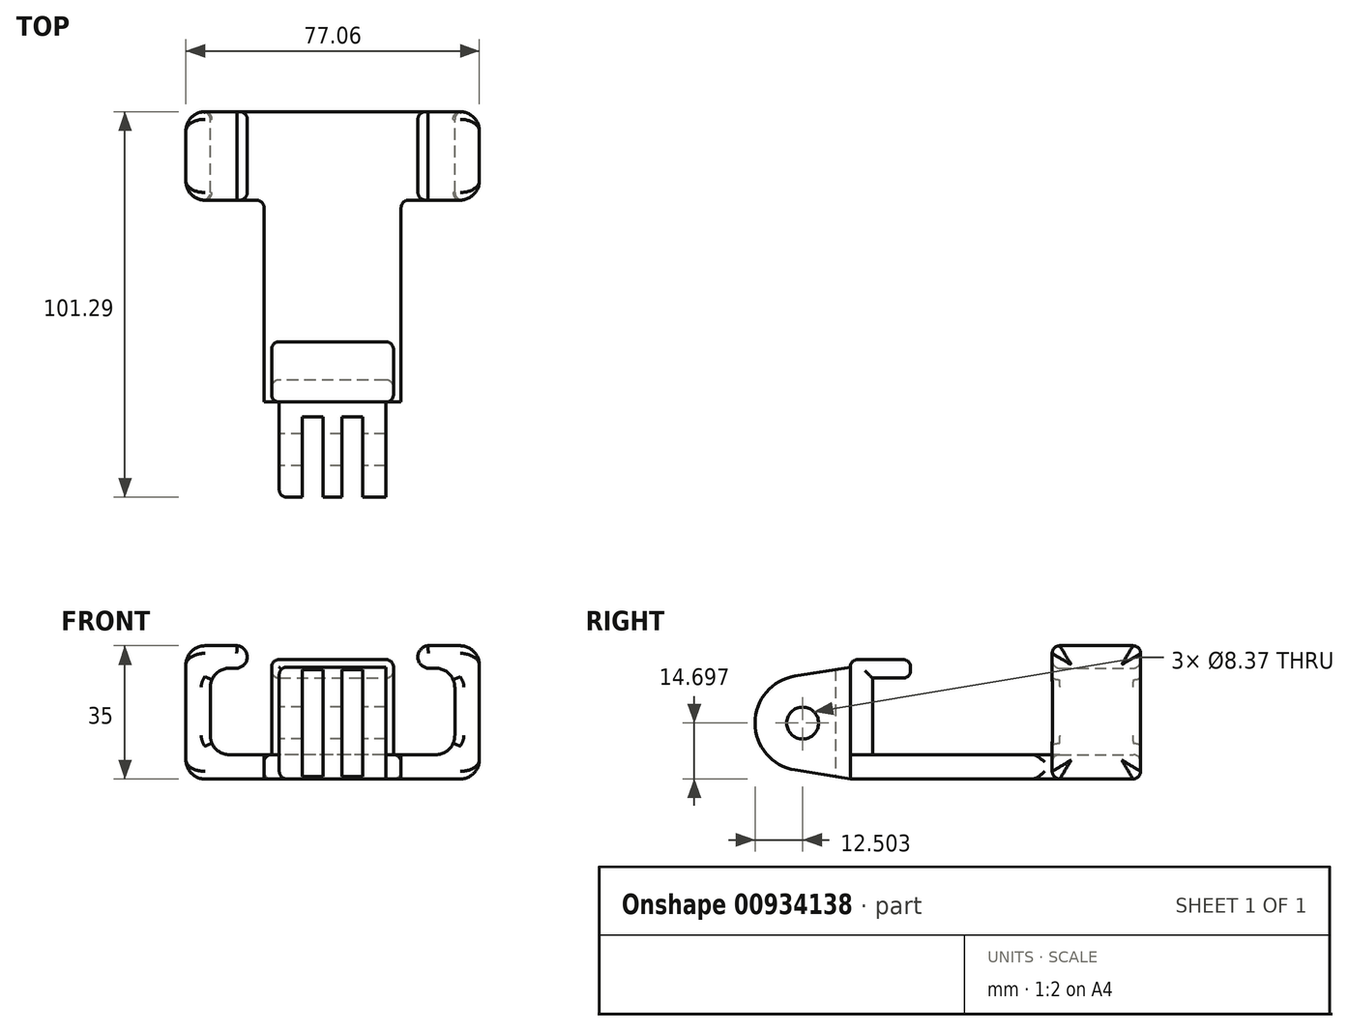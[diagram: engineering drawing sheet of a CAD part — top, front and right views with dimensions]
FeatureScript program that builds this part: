
annotation { "Feature Type Name" : "Feature", "Feature Type Description" : "" }
export const myFeature = defineFeature(function(context is Context, id is Id, definition is map)
    precondition{}
    {
        {
            var Q0;
            Q0=qCreatedBy(makeId("Top.planeOp"),FACE);
            var sketch = newSketch(context, id + "F0", { "sketchPlane" : qUnion([Q0])});
            skLineSegment(sketch, "E0", {"start": v(0, -65.26) * mm, "end": v(18, -65.26) * mm});
            skLineSegment(sketch, "E1", {"start": v(18, -65.26) * mm, "end": v(18, -12.2) * mm});
            skLineSegment(sketch, "E2", {"start": v(18, -12.2) * mm, "end": v(38.53, -12.2) * mm});
            skLineSegment(sketch, "E3", {"start": v(38.53, -12.2) * mm, "end": v(38.53, 11.03) * mm});
            skLineSegment(sketch, "E4", {"start": v(38.53, 11.03) * mm, "end": v(0, 11.03) * mm});
            skLineSegment(sketch, "E5.MirrorCS", {"start": v(-38.53, 11.03) * mm, "end": v(0, 11.03) * mm});
            skLineSegment(sketch, "E6.MirrorCS", {"start": v(-38.53, -12.2) * mm, "end": v(-38.53, 11.03) * mm});
            skLineSegment(sketch, "E7.MirrorCS", {"start": v(-18, -12.2) * mm, "end": v(-38.53, -12.2) * mm});
            skLineSegment(sketch, "E8.MirrorCS", {"start": v(-18, -65.26) * mm, "end": v(-18, -12.2) * mm});
            skLineSegment(sketch, "E9.MirrorCS", {"start": v(0, -65.26) * mm, "end": v(-18, -65.26) * mm});
            skSolve(sketch);
        }
        {
            var Q0;
            Q0=makeQuery(id+"F0.imprint","IMPRINT",FACE,{"disambiguationData":[TD([[makeQuery(id+"F0.imprint","IMPRINT",EDGE,{"derivedFrom":sQuery(id+"F0.wireOp",EDGE,"E0")}),1.0]])]});
            extrude(context, id + "F1", {"entities" : qUnion([Q0]), "depth" : 35 * mm, "offsetDistance" : 25 * mm});
        }
        {
            var Q0;
            Q0=makeQuery(id+"F1.opExtrude","SWEPT_FACE",FACE,{"disambiguationData":[OSD([sQuery(id+"F0.wireOp",EDGE,"E4"),sQuery(id+"F0.wireOp",EDGE,"E5.MirrorCS")])]});
            var sketch = newSketch(context, id + "F2", { "sketchPlane" : qUnion([Q0])});
            skLineSegment(sketch, "E10", {"start": v(-25.39, 29.08) * mm, "end": v(-27.11, 29.08) * mm});
            skLineSegment(sketch, "E11", {"start": v(-32.11, 24.08) * mm, "end": v(-32.11, 11.4) * mm});
            skLineSegment(sketch, "E12", {"start": v(-27.11, 6.4) * mm, "end": v(0, 6.4) * mm});
            skLineSegment(sketch, "E13.MirrorCS", {"start": v(32.11, 24.08) * mm, "end": v(32.11, 11.4) * mm});
            skLineSegment(sketch, "E14.MirrorCS", {"start": v(25.39, 29.08) * mm, "end": v(27.11, 29.08) * mm});
            skLineSegment(sketch, "E15.MirrorCS", {"start": v(27.11, 6.4) * mm, "end": v(0, 6.4) * mm});
            skArc(sketch, "E16", {"start": v(-25.39, 29.08) * mm, "mid": v(-22.43, 31.88) * mm, "end": v(-25.05, 35) * mm});
            skLineSegment(sketch, "E17", {"start": v(0, 0) * mm, "end": v(0, 33.52) * mm, "construction": true});
            skArc(sketch, "E18.MirrorCS", {"start": v(25.39, 29.08) * mm, "mid": v(22.43, 31.88) * mm, "end": v(25.05, 35) * mm});
            skPoint(sketch, "E19.visualSharp", {"position": v(-32.11, 29.08) * mm});
            skArc(sketch, "E19.filletArc", {"start": v(-27.11, 29.08) * mm, "mid": v(-30.65, 27.62) * mm, "end": v(-32.11, 24.08) * mm});
            skPoint(sketch, "E20.visualSharp", {"position": v(32.11, 29.08) * mm});
            skArc(sketch, "E20.filletArc", {"start": v(32.11, 24.08) * mm, "mid": v(30.65, 27.62) * mm, "end": v(27.11, 29.08) * mm});
            skPoint(sketch, "E21.visualSharp", {"position": v(32.11, 6.4) * mm});
            skArc(sketch, "E21.filletArc", {"start": v(27.11, 6.4) * mm, "mid": v(30.65, 7.86) * mm, "end": v(32.11, 11.4) * mm});
            skPoint(sketch, "E22.visualSharp", {"position": v(-32.11, 6.4) * mm});
            skArc(sketch, "E22.filletArc", {"start": v(-32.11, 11.4) * mm, "mid": v(-30.65, 7.86) * mm, "end": v(-27.11, 6.4) * mm});
            skLineSegment(sketch, "E23", {"start": v(25.05, 35) * mm, "end": v(30.53, 35) * mm});
            skLineSegment(sketch, "E24", {"start": v(38.53, 27) * mm, "end": v(38.53, 8) * mm});
            skLineSegment(sketch, "E25", {"start": v(30.53, 0) * mm, "end": v(0, 0) * mm});
            skLineSegment(sketch, "E26", {"start": v(0, 0) * mm, "end": v(-30.53, 0) * mm});
            skLineSegment(sketch, "E27", {"start": v(-38.53, 8) * mm, "end": v(-38.53, 27) * mm});
            skLineSegment(sketch, "E28", {"start": v(-30.53, 35) * mm, "end": v(-25.05, 35) * mm});
            skPoint(sketch, "E29.visualSharp", {"position": v(38.53, 35) * mm});
            skArc(sketch, "E29.filletArc", {"start": v(38.53, 27) * mm, "mid": v(36.19, 32.66) * mm, "end": v(30.53, 35) * mm});
            skPoint(sketch, "E30.visualSharp", {"position": v(-38.53, 35) * mm});
            skArc(sketch, "E30.filletArc", {"start": v(-30.53, 35) * mm, "mid": v(-36.19, 32.66) * mm, "end": v(-38.53, 27) * mm});
            skPoint(sketch, "E31.visualSharp", {"position": v(-38.53, 0) * mm});
            skArc(sketch, "E31.filletArc", {"start": v(-38.53, 8) * mm, "mid": v(-36.19, 2.34) * mm, "end": v(-30.53, 0) * mm});
            skPoint(sketch, "E32.visualSharp", {"position": v(38.53, 0) * mm});
            skArc(sketch, "E32.filletArc", {"start": v(30.53, 0) * mm, "mid": v(36.19, 2.34) * mm, "end": v(38.53, 8) * mm});
            skSolve(sketch);
        }
        {
            var Q0;
            Q0=makeQuery(id+"F2.imprint","IMPRINT",FACE,{"disambiguationData":[TD([[makeQuery(id+"F2.imprint","IMPRINT",EDGE,{"derivedFrom":sQuery(id+"F2.wireOp",EDGE,"E10")}),1.0]])]});
            extrude(context, id + "F3", {"entities" : qUnion([Q0]), "operationType" : NewBodyOperationType.REMOVE, "endBound" : BoundingType.THROUGH_ALL, "oppositeDirection" : true, "depth" : 25 * mm, "offsetDistance" : 25 * mm});
        }
        {
            var Q0;
            Q0=makeQuery(id+"F1.opExtrude","SWEPT_FACE",FACE,{"disambiguationData":[OSD([sQuery(id+"F0.wireOp",EDGE,"E3")])]});
            var Q1;
            Q1=makeQuery(id+"F1.opExtrude","SWEPT_FACE",FACE,{"disambiguationData":[OSD([sQuery(id+"F0.wireOp",EDGE,"E6.MirrorCS")])]});
            fillet(context, id + "F4", {"entities" : qUnion([Q0, Q1]), "radius" : 5 * mm, "tangentPropagation" : true, "allowEdgeOverflow" : false});
        }
        {
            var Q0;
            Q0=makeQuery(id+"F1.opExtrude","SWEPT_FACE",FACE,{"disambiguationData":[OSD([sQuery(id+"F0.wireOp",EDGE,"E4"),sQuery(id+"F0.wireOp",EDGE,"E5.MirrorCS")])]});
            var Q1;
            Q1=makeQuery(id+"F1.opExtrude","SWEPT_FACE",FACE,{"disambiguationData":[OSD([sQuery(id+"F0.wireOp",EDGE,"E2")])]});
            var Q2;
            Q2=makeQuery(id+"F1.opExtrude","SWEPT_FACE",FACE,{"disambiguationData":[OSD([sQuery(id+"F0.wireOp",EDGE,"E7.MirrorCS")])]});
            fillet(context, id + "F5", {"entities" : qUnion([Q0, Q1, Q2]), "radius" : 2 * mm, "tangentPropagation" : true, "allowEdgeOverflow" : false});
        }
        {
            var Q0;
            Q0=makeQuery(id+"F3.boolean.opBoolean","COPY",FACE,{"derivedFrom":makeQuery(id+"F3.opExtrude","SWEPT_FACE",FACE,{"disambiguationData":[OSD([sQuery(id+"F2.wireOp",EDGE,"E12"),sQuery(id+"F2.wireOp",EDGE,"E15.MirrorCS")])]})});
            var sketch = newSketch(context, id + "F6", { "sketchPlane" : qUnion([Q0])});
            skLineSegment(sketch, "E33.bottom", {"start": v(16, -65.26) * mm, "end": v(-16, -65.26) * mm});
            skLineSegment(sketch, "E33.top", {"start": v(16, -59.42) * mm, "end": v(-16, -59.42) * mm});
            skLineSegment(sketch, "E33.left", {"start": v(16, -65.26) * mm, "end": v(16, -59.42) * mm});
            skLineSegment(sketch, "E33.right", {"start": v(-16, -65.26) * mm, "end": v(-16, -59.42) * mm});
            skSolve(sketch);
        }
        {
            var Q0;
            Q0=makeQuery(id+"F6.imprint","IMPRINT",FACE,{"disambiguationData":[TD([[makeQuery(id+"F6.imprint","IMPRINT",EDGE,{"derivedFrom":sQuery(id+"F6.wireOp",EDGE,"E33.bottom")}),1.0]])]});
            extrude(context, id + "F7", {"entities" : qUnion([Q0]), "operationType" : NewBodyOperationType.ADD, "depth" : 25 * mm, "offsetDistance" : 25 * mm});
        }
        {
            var Q0;
            Q0=makeQuery(id+"F7.opExtrude","SWEPT_FACE",FACE,{"disambiguationData":[OSD([sQuery(id+"F6.wireOp",EDGE,"E33.top")])]});
            var sketch = newSketch(context, id + "F8", { "sketchPlane" : qUnion([Q0])});
            skLineSegment(sketch, "E34.bottom", {"start": v(16, 31.4) * mm, "end": v(-16, 31.4) * mm});
            skLineSegment(sketch, "E34.top", {"start": v(16, 26.5) * mm, "end": v(-16, 26.5) * mm});
            skLineSegment(sketch, "E34.left", {"start": v(16, 31.4) * mm, "end": v(16, 26.5) * mm});
            skLineSegment(sketch, "E34.right", {"start": v(-16, 31.4) * mm, "end": v(-16, 26.5) * mm});
            skSolve(sketch);
        }
        {
            var Q0;
            Q0=makeQuery(id+"F8.imprint","IMPRINT",FACE,{"disambiguationData":[TD([[makeQuery(id+"F8.imprint","IMPRINT",EDGE,{"derivedFrom":sQuery(id+"F8.wireOp",EDGE,"E34.bottom")}),-1.0]])]});
            extrude(context, id + "F9", {"entities" : qUnion([Q0]), "operationType" : NewBodyOperationType.ADD, "depth" : 10 * mm, "offsetDistance" : 25 * mm});
        }
        {
            var Q0;
            Q0=makeQuery(id+"F9.opExtrude","SWEPT_EDGE",EDGE,{"disambiguationData":[OSD([sQuery(id+"F0.wireOp",EDGE,"E8.MirrorCS"),sQuery(id+"F2.wireOp",EDGE,"E12"),sQuery(id+"F2.wireOp",EDGE,"E15.MirrorCS"),sQuery(id+"F6.wireOp",EDGE,"E33.top"),sQuery(id+"F6.wireOp",EDGE,"E33.right"),sQuery(id+"F8.wireOp",EDGE,"E34.top"),sQuery(id+"F8.wireOp",EDGE,"E34.left")])]});
            var Q1;
            Q1=makeQuery(id+"F9.opExtrude","CAP_EDGE",EDGE,{"disambiguationData":[OSD([sQuery(id+"F8.wireOp",EDGE,"E34.left")])],"isStart":false});
            var Q2;
            Q2=makeQuery(id+"F9.boolean.opBoolean","MERGE",EDGE,{"derivedFrom":[makeQuery(id+"F7.opExtrude","CAP_EDGE",EDGE,{"disambiguationData":[OSD([sQuery(id+"F6.wireOp",EDGE,"E33.right")])],"isStart":false}),makeQuery(id+"F9.opExtrude","SWEPT_EDGE",EDGE,{"disambiguationData":[OSD([sQuery(id+"F8.wireOp",EDGE,"E34.bottom"),sQuery(id+"F8.wireOp",EDGE,"E34.left")])]})]});
            var Q3;
            Q3=makeQuery(id+"F7.opExtrude","SWEPT_EDGE",EDGE,{"disambiguationData":[OSD([sQuery(id+"F6.wireOp",EDGE,"E33.bottom"),sQuery(id+"F6.wireOp",EDGE,"E33.right")])]});
            var Q4;
            Q4=makeQuery(id+"F7.opExtrude","SWEPT_EDGE",EDGE,{"disambiguationData":[OSD([sQuery(id+"F0.wireOp",EDGE,"E8.MirrorCS"),sQuery(id+"F2.wireOp",EDGE,"E12"),sQuery(id+"F2.wireOp",EDGE,"E15.MirrorCS"),sQuery(id+"F6.wireOp",EDGE,"E33.top"),sQuery(id+"F6.wireOp",EDGE,"E33.right")])]});
            var Q5;
            Q5=makeQuery(id+"F9.boolean.opBoolean","MERGE",EDGE,{"derivedFrom":[makeQuery(id+"F7.opExtrude","CAP_EDGE",EDGE,{"disambiguationData":[OSD([sQuery(id+"F6.wireOp",EDGE,"E33.left")])],"isStart":false}),makeQuery(id+"F9.opExtrude","SWEPT_EDGE",EDGE,{"disambiguationData":[OSD([sQuery(id+"F8.wireOp",EDGE,"E34.bottom"),sQuery(id+"F8.wireOp",EDGE,"E34.right")])]})]});
            var Q6;
            Q6=makeQuery(id+"F9.opExtrude","CAP_EDGE",EDGE,{"disambiguationData":[OSD([sQuery(id+"F8.wireOp",EDGE,"E34.right")])],"isStart":false});
            var Q7;
            Q7=makeQuery(id+"F7.opExtrude","SWEPT_EDGE",EDGE,{"disambiguationData":[OSD([sQuery(id+"F6.wireOp",EDGE,"E33.bottom"),sQuery(id+"F6.wireOp",EDGE,"E33.left")])]});
            var Q8;
            Q8=makeQuery(id+"F7.opExtrude","SWEPT_EDGE",EDGE,{"disambiguationData":[OSD([sQuery(id+"F0.wireOp",EDGE,"E1"),sQuery(id+"F2.wireOp",EDGE,"E12"),sQuery(id+"F2.wireOp",EDGE,"E15.MirrorCS"),sQuery(id+"F6.wireOp",EDGE,"E33.top"),sQuery(id+"F6.wireOp",EDGE,"E33.left")])]});
            var Q9;
            Q9=makeQuery(id+"F9.opExtrude","SWEPT_EDGE",EDGE,{"disambiguationData":[OSD([sQuery(id+"F0.wireOp",EDGE,"E1"),sQuery(id+"F2.wireOp",EDGE,"E12"),sQuery(id+"F2.wireOp",EDGE,"E15.MirrorCS"),sQuery(id+"F6.wireOp",EDGE,"E33.top"),sQuery(id+"F6.wireOp",EDGE,"E33.left"),sQuery(id+"F8.wireOp",EDGE,"E34.top"),sQuery(id+"F8.wireOp",EDGE,"E34.right")])]});
            var Q10;
            Q10=makeQuery(id+"F7.opExtrude","CAP_EDGE",EDGE,{"disambiguationData":[OSD([sQuery(id+"F6.wireOp",EDGE,"E33.bottom")])],"isStart":false});
            var Q11;
            Q11=makeQuery(id+"F9.opExtrude","CAP_EDGE",EDGE,{"disambiguationData":[OSD([sQuery(id+"F8.wireOp",EDGE,"E34.bottom")])],"isStart":false});
            var Q12;
            Q12=makeQuery(id+"F9.opExtrude","CAP_EDGE",EDGE,{"disambiguationData":[OSD([sQuery(id+"F8.wireOp",EDGE,"E34.top")])],"isStart":false});
            fillet(context, id + "F10", {"entities" : qUnion([Q0, Q1, Q2, Q3, Q4, Q5, Q6, Q7, Q8, Q9, Q10, Q11, Q12]), "radius" : 2 * mm, "tangentPropagation" : true, "allowEdgeOverflow" : false});
        }
        {
            var Q0;
            Q0=makeQuery(id+"F7.boolean.opBoolean","MERGE",FACE,{"derivedFrom":[makeQuery(id+"F1.opExtrude","SWEPT_FACE",FACE,{"disambiguationData":[OSD([sQuery(id+"F0.wireOp",EDGE,"E0"),sQuery(id+"F0.wireOp",EDGE,"E9.MirrorCS")])]}),makeQuery(id+"F7.opExtrude","SWEPT_FACE",FACE,{"disambiguationData":[OSD([sQuery(id+"F6.wireOp",EDGE,"E33.bottom")])]})]});
            var sketch = newSketch(context, id + "F11", { "sketchPlane" : qUnion([Q0])});
            skLineSegment(sketch, "E35.bottom", {"start": v(-14, 29.4) * mm, "end": v(14, 29.4) * mm});
            skLineSegment(sketch, "E35.top", {"start": v(-14, 0) * mm, "end": v(14, 0) * mm});
            skLineSegment(sketch, "E35.left", {"start": v(-14, 29.4) * mm, "end": v(-14, 0) * mm});
            skLineSegment(sketch, "E35.right", {"start": v(14, 29.4) * mm, "end": v(14, 0) * mm});
            skSolve(sketch);
        }
        {
            var Q0;
            {var subQ8=sQuery(id+"F11.wireOp",EDGE,"E35.bottom");Q0=makeQuery(id+"F11.imprint","IMPRINT",FACE,{"disambiguationData":[TD([[makeQuery(id+"F11.imprint","IMPRINT",EDGE,{"derivedFrom":subQ8}),1.0]])]});}
            extrude(context, id + "F12", {"entities" : qUnion([Q0]), "operationType" : NewBodyOperationType.ADD, "depth" : 25 * mm, "offsetDistance" : 25 * mm});
        }
        {
            var Q0;
            Q0=makeQuery(id+"F12.opExtrude","SWEPT_FACE",FACE,{"disambiguationData":[OSD([sQuery(id+"F11.wireOp",EDGE,"E35.right")])]});
            var sketch = newSketch(context, id + "F13", { "sketchPlane" : qUnion([Q0])});
            skArc(sketch, "E36", {"start": v(-79.76, 27.04) * mm, "mid": v(-90.26, 14.7) * mm, "end": v(-79.76, 2.36) * mm});
            skPoint(sketch, "E36.centerSnap0", {"position": v(-90.26, 14.7) * mm});
            skPoint(sketch, "E36.centerSnap1", {"position": v(-77.76, 0) * mm});
            skLineSegment(sketch, "E37", {"start": v(-65.26, 29.4) * mm, "end": v(-79.76, 27.04) * mm});
            skPoint(sketch, "E38.endSnap0", {"position": v(-65.26, 2.2) * mm});
            skLineSegment(sketch, "E39", {"start": v(-79.76, 2.36) * mm, "end": v(-65.26, 0) * mm});
            skPoint(sketch, "E38.end.orphan", {"position": v(-77.76, 2.2) * mm});
            skSolve(sketch);
        }
        {
            var Q0;
            {var subQ0=sQuery(id+"F13.wireOp",EDGE,"E37");Q0=makeQuery(id+"F13.imprint","IMPRINT",FACE,{"disambiguationData":[TD([[makeQuery(id+"F13.imprint","IMPRINT",EDGE,{"derivedFrom":subQ0}),-1.0]])]});}
            var Q1;
            {var subQ0=sQuery(id+"F13.wireOp",EDGE,"E39");Q1=makeQuery(id+"F13.imprint","IMPRINT",FACE,{"disambiguationData":[TD([[makeQuery(id+"F13.imprint","IMPRINT",EDGE,{"derivedFrom":subQ0}),-1.0]])]});}
            extrude(context, id + "F14", {"entities" : qUnion([Q0, Q1]), "operationType" : NewBodyOperationType.REMOVE, "endBound" : BoundingType.THROUGH_ALL, "oppositeDirection" : true, "depth" : 25 * mm, "offsetDistance" : 25 * mm});
        }
        {
            var Q0;
            Q0=qCreatedBy(makeId("Top.planeOp"),FACE);
            var sketch = newSketch(context, id + "F15", { "sketchPlane" : qUnion([Q0])});
            skLineSegment(sketch, "E40", {"start": v(0, -65.45) * mm, "end": v(0, -92.28) * mm, "construction": true});
            skLineSegment(sketch, "E41.bottom", {"start": v(0, -69.16) * mm, "end": v(-2.44, -69.16) * mm});
            skLineSegment(sketch, "E41.top", {"start": v(0, -93.62) * mm, "end": v(-2.44, -93.62) * mm});
            skLineSegment(sketch, "E41.left", {"start": v(0, -69.16) * mm, "end": v(0, -93.62) * mm});
            skLineSegment(sketch, "E41.right", {"start": v(-2.44, -69.16) * mm, "end": v(-2.44, -93.62) * mm});
            skLineSegment(sketch, "E42.bottom", {"start": v(-2.44, -69.16) * mm, "end": v(-7.94, -69.16) * mm});
            skLineSegment(sketch, "E42.top", {"start": v(-2.44, -93.62) * mm, "end": v(-7.94, -93.62) * mm});
            skLineSegment(sketch, "E42.right", {"start": v(-7.94, -69.16) * mm, "end": v(-7.94, -93.62) * mm});
            skLineSegment(sketch, "E43.MirrorCS", {"start": v(2.44, -69.16) * mm, "end": v(7.94, -69.16) * mm});
            skLineSegment(sketch, "E44.MirrorCS", {"start": v(7.94, -69.16) * mm, "end": v(7.94, -93.62) * mm});
            skLineSegment(sketch, "E45.MirrorCS", {"start": v(2.44, -69.16) * mm, "end": v(2.44, -93.62) * mm});
            skLineSegment(sketch, "E46.MirrorCS", {"start": v(2.44, -93.62) * mm, "end": v(7.94, -93.62) * mm});
            skSolve(sketch);
        }
        {
            var Q0;
            Q0=makeQuery(id+"F15.imprint","IMPRINT",FACE,{"disambiguationData":[TD([[makeQuery(id+"F15.imprint","IMPRINT",EDGE,{"derivedFrom":sQuery(id+"F15.wireOp",EDGE,"E42.bottom")}),1.0]])]});
            var Q1;
            Q1=makeQuery(id+"F15.imprint","IMPRINT",FACE,{"disambiguationData":[TD([[makeQuery(id+"F15.imprint","IMPRINT",EDGE,{"derivedFrom":sQuery(id+"F15.wireOp",EDGE,"E43.MirrorCS")}),-1.0]])]});
            extrude(context, id + "F16", {"entities" : qUnion([Q0, Q1]), "operationType" : NewBodyOperationType.REMOVE, "endBound" : BoundingType.THROUGH_ALL, "depth" : 25 * mm, "offsetDistance" : 25 * mm});
        }
        {
            var Q0;
            Q0=makeQuery(id+"F12.opExtrude","SWEPT_FACE",FACE,{"disambiguationData":[OSD([sQuery(id+"F11.wireOp",EDGE,"E35.left")])]});
            var sketch = newSketch(context, id + "F17", { "sketchPlane" : qUnion([Q0])});
            skCircle(sketch, "E47", {"center": v(77.76, 14.7) * mm, "radius": 4.19 * mm});
            skSolve(sketch);
        }
        {
            var Q0;
            Q0=makeQuery(id+"F17.imprint","IMPRINT",FACE,{"disambiguationData":[TD([[makeQuery(id+"F17.imprint","IMPRINT",EDGE,{"derivedFrom":sQuery(id+"F17.wireOp",EDGE,"E47")}),1.0]])]});
            extrude(context, id + "F18", {"entities" : qUnion([Q0]), "operationType" : NewBodyOperationType.REMOVE, "endBound" : BoundingType.THROUGH_ALL, "oppositeDirection" : true, "depth" : 25 * mm, "offsetDistance" : 25 * mm});
        }
        {
            var Q0;
            Q0=makeQuery(id+"F14.boolean.opBoolean","INTERSECT",EDGE,{"derivedFrom":[makeQuery(id+"F12.opExtrude","SWEPT_FACE",FACE,{"disambiguationData":[OSD([sQuery(id+"F11.wireOp",EDGE,"E35.left")])]}),makeQuery(id+"F14.opExtrude","SWEPT_FACE",FACE,{"disambiguationData":[OSD([sQuery(id+"F13.wireOp",EDGE,"E39")])]})]});
            var Q1;
            Q1=makeQuery(id+"F14.boolean.opBoolean","COPY",EDGE,{"derivedFrom":makeQuery(id+"F14.opExtrude","CAP_EDGE",EDGE,{"disambiguationData":[OSD([sQuery(id+"F13.wireOp",EDGE,"E37")])],"isStart":true})});
            fillet(context, id + "F19", {"entities" : qUnion([Q0, Q1]), "radius" : 2 * mm, "tangentPropagation" : true, "allowEdgeOverflow" : false});
        }
    });
